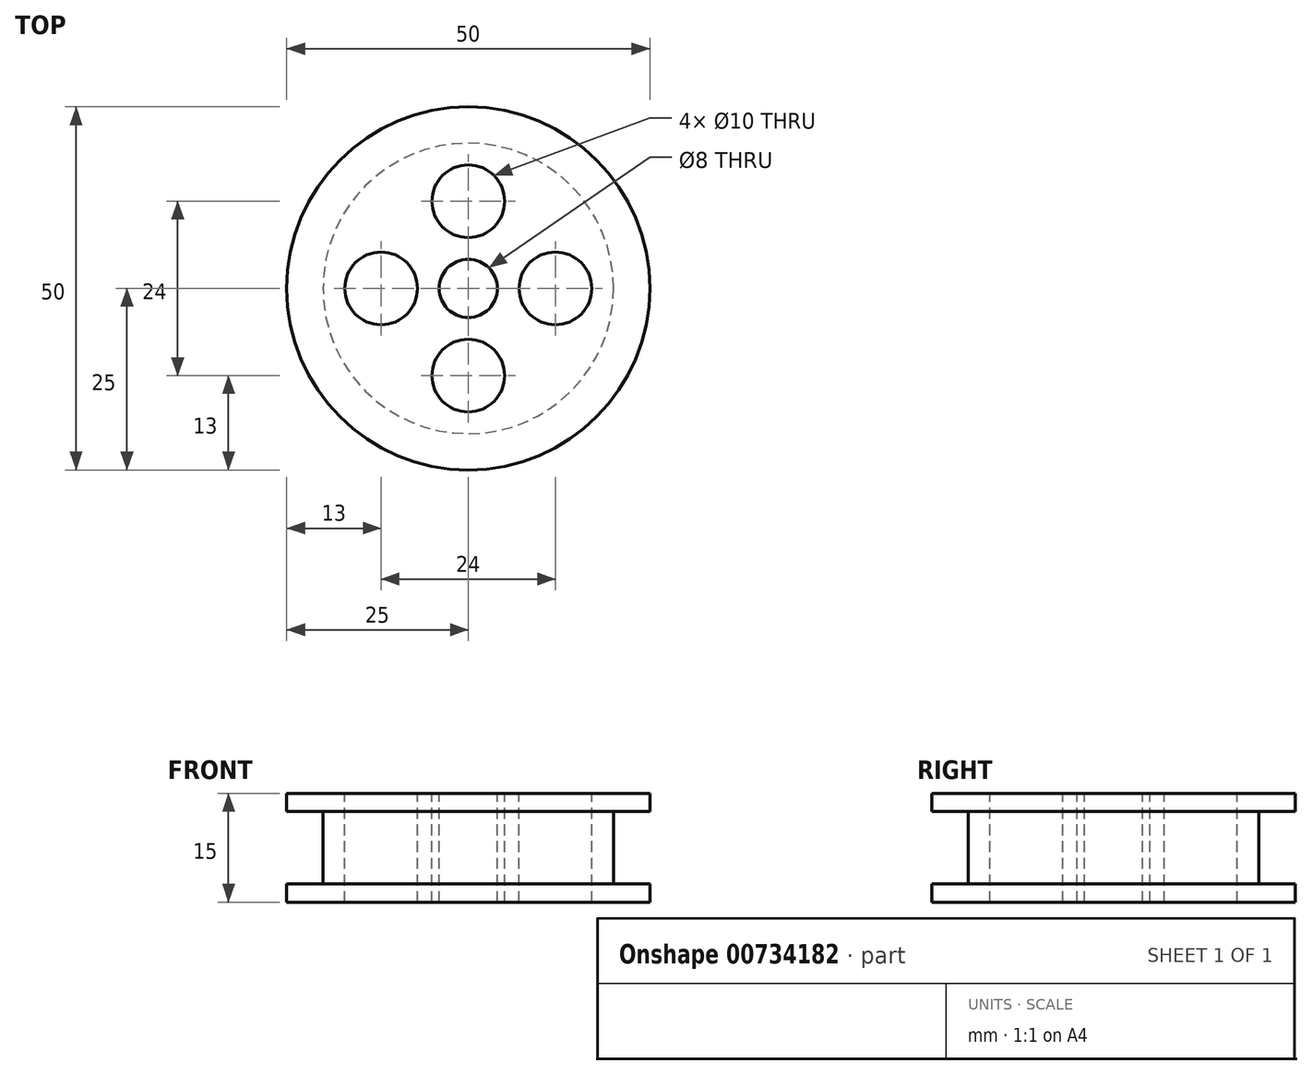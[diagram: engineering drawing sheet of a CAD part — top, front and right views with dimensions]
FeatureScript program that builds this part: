
annotation { "Feature Type Name" : "Feature", "Feature Type Description" : "" }
export const myFeature = defineFeature(function(context is Context, id is Id, definition is map)
    precondition{}
    {
        {
            var Q0;
            Q0=qCreatedBy(makeId("Front.planeOp"),FACE);
            var sketch = newSketch(context, id + "F0", { "sketchPlane" : qUnion([Q0])});
            skLineSegment(sketch, "E0", {"start": v(0, 7.5) * mm, "end": v(0, -7.5) * mm});
            skLineSegment(sketch, "E1", {"start": v(0, -7.5) * mm, "end": v(-25, -7.5) * mm});
            skLineSegment(sketch, "E2", {"start": v(-25, -7.5) * mm, "end": v(-25, -5) * mm});
            skLineSegment(sketch, "E3", {"start": v(-25, -5) * mm, "end": v(-20, -5) * mm});
            skLineSegment(sketch, "E4", {"start": v(-20, -5) * mm, "end": v(-20, 5) * mm});
            skLineSegment(sketch, "E5", {"start": v(-20, 5) * mm, "end": v(-25, 5) * mm});
            skLineSegment(sketch, "E6", {"start": v(-25, 5) * mm, "end": v(-25, 7.5) * mm});
            skLineSegment(sketch, "E7", {"start": v(-25, 7.5) * mm, "end": v(0, 7.5) * mm});
            skLineSegment(sketch, "E8", {"start": v(0, 0) * mm, "end": v(-69.4, 0) * mm, "construction": true});
            skPoint(sketch, "E8.endSnap0", {"position": v(-20, 0) * mm});
            skSolve(sketch);
        }
        {
            var Q0;
            Q0 = qSketchRegion(id + "F0", true);
            var Q1;
            Q1=sQuery(id+"F0.wireOp",EDGE,"E0");
            revolve(context, id + "F1", {"surfaceOperationType" : NewSurfaceOperationType.NEW, "entities" : qUnion([Q0]), "axis" : qUnion([Q1]), "revolveType" : RevolveType.FULL});
        }
        {
            var Q0;
            Q0=makeQuery(id+"F1.opRevolve","SWEPT_FACE",FACE,{"disambiguationData":[OSD([sQuery(id+"F0.wireOp",EDGE,"E7")])]});
            var sketch = newSketch(context, id + "F2", { "sketchPlane" : qUnion([Q0])});
            skCircle(sketch, "E9", {"center": v(0, 0) * mm, "radius": 4 * mm});
            skSolve(sketch);
        }
        {
            var Q0;
            Q0 = qSketchRegion(id + "F2", true);
            extrude(context, id + "F3", {"entities" : qUnion([Q0]), "operationType" : NewBodyOperationType.REMOVE, "endBound" : BoundingType.THROUGH_ALL, "oppositeDirection" : true, "depth" : 25 * mm, "offsetDistance" : 25 * mm});
        }
        {
            var Q0;
            Q0=makeQuery(id+"F1.opRevolve","SWEPT_FACE",FACE,{"disambiguationData":[OSD([sQuery(id+"F0.wireOp",EDGE,"E7")])]});
            var sketch = newSketch(context, id + "F4", { "sketchPlane" : qUnion([Q0])});
            skLineSegment(sketch, "E10", {"start": v(0, 25) * mm, "end": v(0, -25) * mm, "construction": true});
            skLineSegment(sketch, "E11", {"start": v(-25, 0) * mm, "end": v(25, 0) * mm, "construction": true});
            skCircle(sketch, "E12", {"center": v(-12, 0) * mm, "radius": 5 * mm});
            skCircle(sketch, "E13", {"center": v(0, 12) * mm, "radius": 5 * mm});
            skCircle(sketch, "E14", {"center": v(12, 0) * mm, "radius": 5 * mm});
            skCircle(sketch, "E15", {"center": v(0, -12) * mm, "radius": 5 * mm});
            skSolve(sketch);
        }
        {
            var Q0;
            Q0 = qSketchRegion(id + "F4", true);
            extrude(context, id + "F5", {"entities" : qUnion([Q0]), "operationType" : NewBodyOperationType.REMOVE, "endBound" : BoundingType.THROUGH_ALL, "oppositeDirection" : true, "depth" : 25 * mm, "offsetDistance" : 25 * mm});
        }
    });
